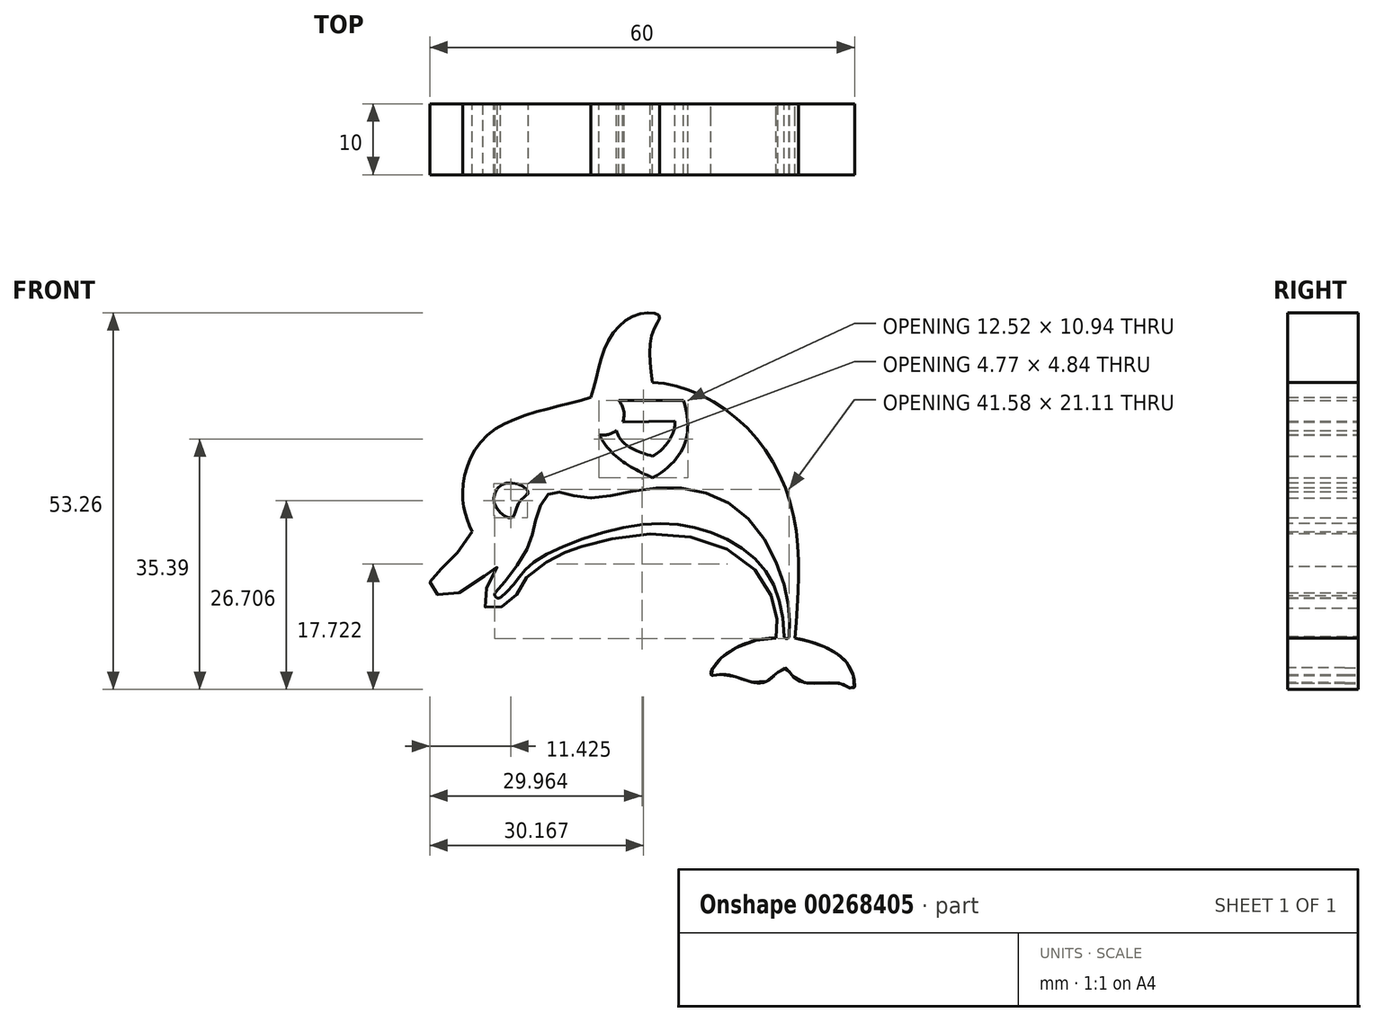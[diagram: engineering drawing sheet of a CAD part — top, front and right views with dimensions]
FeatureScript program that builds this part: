
annotation { "Feature Type Name" : "Feature", "Feature Type Description" : "" }
export const myFeature = defineFeature(function(context is Context, id is Id, definition is map)
    precondition{}
    {
        {
            var Q0;
            Q0=qCreatedBy(makeId("Front.planeOp"),FACE);
            var sketch = newSketch(context, id + "F0", { "sketchPlane" : qUnion([Q0])});
            skFitSpline(sketch, "E0", {"points": [v(-25.48, -7.62) * mm, v(-26.83, -2.44) * mm, v(-23.22, 6.13) * mm, v(-9.56, 11.1) * mm, v(0, 13.5) * mm, v(12.02, 8.3) * mm, v(19.83, -4.92) * mm, v(20.13, -22.67) * mm], "startDerivative": vector(-20.96, 49.8) * mm, "endDerivative": vector(-8.27, -104.1) * mm});
            skFitSpline(sketch, "E1", {"points": [v(20.13, -22.67) * mm, v(25.04, -24.25) * mm, v(28.1, -27.22) * mm, v(28.4, -29.9) * mm, v(26.81, -29.13) * mm, v(20.58, -28.67) * mm, v(18.7, -26.86) * mm, v(15.8, -28.9) * mm, v(10.31, -27.8) * mm, v(8.28, -27.87) * mm, v(9.54, -25.64) * mm, v(17.45, -22.67) * mm], "startDerivative": vector(47.96, -7.58) * mm, "endDerivative": vector(65.5, -3.83) * mm});
            skFitSpline(sketch, "E2", {"points": [v(17.45, -22.67) * mm, v(17.45, -18.89) * mm, v(13.41, -11.98) * mm, v(0.56, -7.9) * mm, v(-10.45, -9.84) * mm, v(-13.1, -10.91) * mm, v(-17.69, -13.98) * mm, v(-19.69, -17.15) * mm, v(-22.7, -18.48) * mm, v(-24.03, -17.48) * mm, v(-21.95, -12.6) * mm, v(-25.5, -15.24) * mm, v(-30.5, -16.46) * mm, v(-31.4, -14.6) * mm, v(-29.09, -12.24) * mm, v(-25.48, -7.62) * mm], "startDerivative": vector(8.68, 59.04) * mm, "endDerivative": vector(47.2, 70.58) * mm});
            skFitSpline(sketch, "E3", {"points": [v(-8.71, 11.37) * mm, v(-6.32, 19.23) * mm, v(-1.91, 23.13) * mm, v(0.96, 22.9) * mm, v(0, 20.55) * mm, v(0, 13.5) * mm], "startDerivative": vector(9.74, 28.22) * mm, "endDerivative": vector(4.25, -32.67) * mm});
            skFitSpline(sketch, "E4", {"points": [v(-19.86, -5.63) * mm, v(-22.28, -3.76) * mm, v(-20.8, -0.77) * mm, v(-17.55, -1.97) * mm, v(-18.89, -3.54) * mm, v(-19.86, -5.63) * mm]});
            skFitSpline(sketch, "E5", {"points": [v(-21.48, -16.92) * mm, v(-19.29, -14.65) * mm, v(-16.83, -11.98) * mm, v(-4.55, -7.12) * mm, v(6.9, -7.28) * mm, v(15.54, -12.61) * mm, v(18.6, -22.41) * mm], "startDerivative": vector(18.5, 14.45) * mm, "endDerivative": vector(1.69, -62.94) * mm});
            skFitSpline(sketch, "E6", {"points": [v(-22.23, -16.28) * mm, v(-17.9, -10.45) * mm, v(-16.42, -5.68) * mm, v(-14.3, -2.06) * mm, v(-9.93, -2.8) * mm, v(0, -1.47) * mm, v(12.5, -4.77) * mm, v(18.89, -16.33) * mm, v(19.3, -22.41) * mm], "startDerivative": vector(23.26, 24.72) * mm, "endDerivative": vector(-1, -48.83) * mm});
            skArc(sketch, "E7", {"start": v(-22.23, -16.28) * mm, "mid": v(-22.1, -16.88) * mm, "end": v(-21.48, -16.92) * mm});
            skArc(sketch, "E8", {"start": v(18.6, -22.41) * mm, "mid": v(18.95, -22.75) * mm, "end": v(19.3, -22.41) * mm});
            skLineSegment(sketch, "E9", {"start": v(-7.29, 10.94) * mm, "end": v(4.36, 10.94) * mm});
            skFitSpline(sketch, "E10", {"points": [v(4.36, 10.94) * mm, v(0, 0) * mm], "startDerivative": vector(4.42, -13.5) * mm, "endDerivative": vector(-14.47, -7.96) * mm});
            skFitSpline(sketch, "E11", {"points": [v(0, 0) * mm, v(-8.04, 7.27) * mm], "startDerivative": vector(-10.14, 4.55) * mm, "endDerivative": vector(-4.16, 11.74) * mm});
            skFitSpline(sketch, "E12", {"points": [v(-5.23, 7.87) * mm, v(0, 3.07) * mm], "startDerivative": vector(0, -8.7) * mm, "endDerivative": vector(9.38, -2.65) * mm});
            skCircle(sketch, "E13", {"center": v(-6.94, 8.95) * mm, "radius": 2.02 * mm});
            skFitSpline(sketch, "E14", {"points": [v(0, 3.07) * mm, v(3.17, 8.04) * mm], "startDerivative": vector(5.21, 2.6) * mm, "endDerivative": vector(-0.73, 5.08) * mm});
            skLineSegment(sketch, "E15", {"start": v(-5.23, 7.87) * mm, "end": v(3.17, 8.04) * mm});
            skSolve(sketch);
        }
        {
            var Q0;
            Q0=makeQuery(id+"F0.imprint","IMPRINT",FACE,{"disambiguationData":[TD([[makeQuery(id+"F0.imprint","IMPRINT",EDGE,{"derivedFrom":sQuery(id+"F0.wireOp",EDGE,"E0")}),-1.0]])]});
            extrude(context, id + "F1", {"entities" : qUnion([Q0]), "depth" : 2 * mm});
        }
        {
            var Q0;
            Q0=makeQuery(id+"F1.opExtrude","CAP_EDGE",EDGE,{"disambiguationData":[OSD([sQuery(id+"F0.wireOp",EDGE,"0B1g3JY2-irfG-N48d-elXG-EENirsOTaup5")])],"isStart":false});
            var Q1;
            Q1=makeQuery(id+"F1.opExtrude","CAP_EDGE",EDGE,{"disambiguationData":[OSD([sQuery(id+"F0.wireOp",EDGE,"0B1g3JY2-irfG-N48d-elXG-EENirsOTaup5")])],"isStart":true});
            var Q2;
            Q2=makeQuery(id+"F1.opExtrude","CAP_EDGE",EDGE,{"disambiguationData":[OSD([sQuery(id+"F0.wireOp",EDGE,"517f8af6-5f73-4e9f-92bd-2466fb0862ea")])],"isStart":false});
            var Q3;
            Q3=makeQuery(id+"F1.opExtrude","CAP_EDGE",EDGE,{"disambiguationData":[OSD([sQuery(id+"F0.wireOp",EDGE,"adb57192-b29e-4277-b92e-72107bf355aa")])],"isStart":false});
            var Q4;
            Q4=makeQuery(id+"F1.opExtrude","CAP_EDGE",EDGE,{"disambiguationData":[OSD([sQuery(id+"F0.wireOp",EDGE,"c88c768c-61d2-49b0-b29e-57fd2349210e")])],"isStart":false});
            var Q5;
            Q5=makeQuery(id+"F1.opExtrude","CAP_EDGE",EDGE,{"disambiguationData":[OSD([sQuery(id+"F0.wireOp",EDGE,"c88c768c-61d2-49b0-b29e-57fd2349210e")])],"isStart":true});
            var Q6;
            Q6=makeQuery(id+"F1.opExtrude","CAP_EDGE",EDGE,{"disambiguationData":[OSD([sQuery(id+"F0.wireOp",EDGE,"adb57192-b29e-4277-b92e-72107bf355aa")])],"isStart":true});
            var Q7;
            Q7=makeQuery(id+"F1.opExtrude","CAP_EDGE",EDGE,{"disambiguationData":[OSD([sQuery(id+"F0.wireOp",EDGE,"517f8af6-5f73-4e9f-92bd-2466fb0862ea")])],"isStart":true});
            var Q8;
            Q8=makeQuery(id+"F1.opExtrude","CAP_EDGE",EDGE,{"disambiguationData":[OSD([sQuery(id+"F0.wireOp",EDGE,"E4")])],"isStart":true});
            var Q9;
            Q9=makeQuery(id+"F1.opExtrude","CAP_EDGE",EDGE,{"disambiguationData":[OSD([sQuery(id+"F0.wireOp",EDGE,"E4")])],"isStart":false});
            chamfer(context, id + "F2", {"entities" : qUnion([Q0, Q1, Q2, Q3, Q4, Q5, Q6, Q7, Q8, Q9]), "width" : .3 * mm, "tangentPropagation" : true});
        }
        {
            var Q0;
            Q0=makeQuery(id+"F1.opExtrude","CAP_EDGE",EDGE,{"disambiguationData":[OSD([sQuery(id+"F0.wireOp",EDGE,"E5")])],"isStart":false});
            var Q1;
            Q1=makeQuery(id+"F1.opExtrude","CAP_EDGE",EDGE,{"disambiguationData":[OSD([sQuery(id+"F0.wireOp",EDGE,"E6")])],"isStart":false});
            var Q2;
            Q2=makeQuery(id+"F1.opExtrude","CAP_EDGE",EDGE,{"disambiguationData":[OSD([sQuery(id+"F0.wireOp",EDGE,"E2")])],"isStart":false});
            var Q3;
            Q3=makeQuery(id+"F1.opExtrude","CAP_EDGE",EDGE,{"disambiguationData":[OSD([sQuery(id+"F0.wireOp",EDGE,"E0")])],"isStart":false});
            var Q4;
            Q4=makeQuery(id+"F1.opExtrude","CAP_EDGE",EDGE,{"disambiguationData":[OSD([sQuery(id+"F0.wireOp",EDGE,"E3")])],"isStart":false});
            var Q5;
            Q5=makeQuery(id+"F1.opExtrude","CAP_EDGE",EDGE,{"disambiguationData":[OSD([sQuery(id+"F0.wireOp",EDGE,"E0")])],"isStart":false});
            var Q6;
            Q6=makeQuery(id+"F1.opExtrude","CAP_EDGE",EDGE,{"disambiguationData":[OSD([sQuery(id+"F0.wireOp",EDGE,"E8")])],"isStart":false});
            var Q7;
            Q7=makeQuery(id+"F1.opExtrude","CAP_EDGE",EDGE,{"disambiguationData":[OSD([sQuery(id+"F0.wireOp",EDGE,"E0")])],"isStart":true});
            var Q8;
            Q8=makeQuery(id+"F1.opExtrude","CAP_EDGE",EDGE,{"disambiguationData":[OSD([sQuery(id+"F0.wireOp",EDGE,"E3")])],"isStart":true});
            var Q9;
            Q9=makeQuery(id+"F1.opExtrude","CAP_EDGE",EDGE,{"disambiguationData":[OSD([sQuery(id+"F0.wireOp",EDGE,"E0")])],"isStart":true});
            var Q10;
            Q10=makeQuery(id+"F1.opExtrude","CAP_EDGE",EDGE,{"disambiguationData":[OSD([sQuery(id+"F0.wireOp",EDGE,"E5")])],"isStart":true});
            var Q11;
            Q11=makeQuery(id+"F1.opExtrude","CAP_EDGE",EDGE,{"disambiguationData":[OSD([sQuery(id+"F0.wireOp",EDGE,"E6")])],"isStart":true});
            var Q12;
            Q12=makeQuery(id+"F1.opExtrude","CAP_EDGE",EDGE,{"disambiguationData":[OSD([sQuery(id+"F0.wireOp",EDGE,"E2")])],"isStart":true});
            fillet(context, id + "F3", {"entities" : qUnion([Q0, Q1, Q2, Q3, Q4, Q5, Q6, Q7, Q8, Q9, Q10, Q11, Q12]), "radius" : .2 * mm, "tangentPropagation" : true, "allowEdgeOverflow" : false});
        }
        {
            var Q0;
            Q0=makeQuery(id+"F1.opExtrude","CAP_EDGE",EDGE,{"disambiguationData":[OSD([sQuery(id+"F0.wireOp",EDGE,"E1")])],"isStart":false});
            var Q1;
            Q1=makeQuery(id+"F1.opExtrude","CAP_EDGE",EDGE,{"disambiguationData":[OSD([sQuery(id+"F0.wireOp",EDGE,"E1")])],"isStart":true});
            fillet(context, id + "F4", {"entities" : qUnion([Q0, Q1]), "radius" : .1 * mm, "tangentPropagation" : true, "allowEdgeOverflow" : false});
        }
        {
            var Q0;
            Q0 = qSketchRegion(id + "F0", true);
            var Q1;
            Q1=makeQuery(id+"F0.imprint","IMPRINT",FACE,{"disambiguationData":[TD([[makeQuery(id+"F0.imprint","IMPRINT",EDGE,{"derivedFrom":sQuery(id+"F0.wireOp",EDGE,"E12")}),1.0]])]});
            extrude(context, id + "F5", {"entities" : qUnion([Q0, Q1]), "operationType" : NewBodyOperationType.ADD, "depth" : 10 * mm});
        }
        {
            var Q0;
            {var subQ0=sQuery(id+"F0.wireOp",EDGE,"E13");var subQ1=sQuery(id+"F0.wireOp",EDGE,"E9");var subQ2=makeQuery(id+"F0.imprint","INTERSECT",VERTEX,{"disambiguationData":[OD(0.0)],"derivedFrom":[subQ1,subQ0]});Q0=makeQuery(id+"F0.imprint","IMPRINT",FACE,{"disambiguationData":[TD([[makeQuery(id+"F0.imprint","IMPRINT",EDGE,{"disambiguationData":[TD([[subQ2,-1.0]])],"derivedFrom":subQ1}),-1.0]])]});}
            var sketch = newSketch(context, id + "F6", { "sketchPlane" : qUnion([Q0])});
            skCircle(sketch, "E16", {"center": v(-6.94, 8.95) * mm, "radius": 2.92 * mm});
            skSolve(sketch);
        }
        {
            var Q0;
            Q0 = qSketchRegion(id + "F6", true);
            extrude(context, id + "F7", {"entities" : qUnion([Q0]), "operationType" : NewBodyOperationType.ADD, "depth" : 10 * mm});
        }
    });
